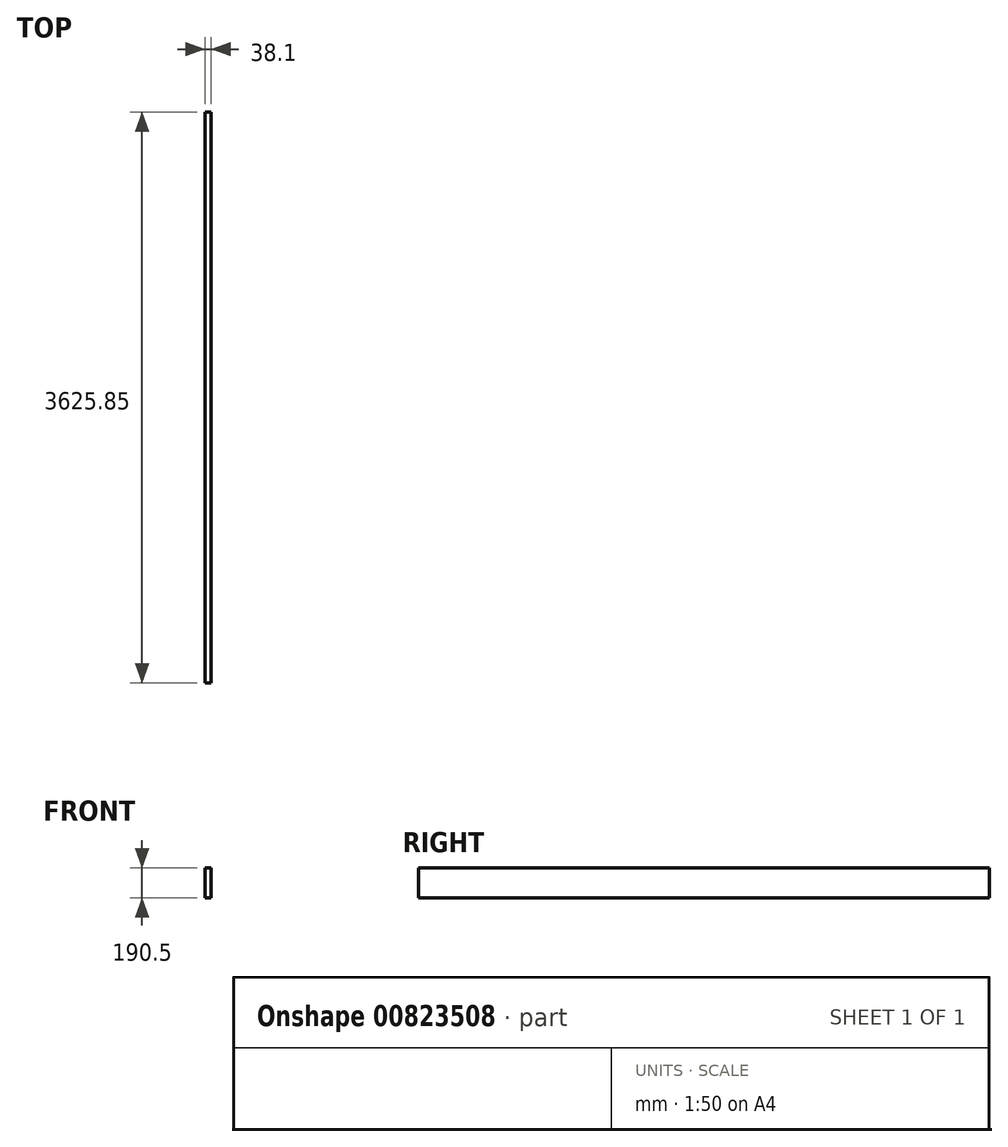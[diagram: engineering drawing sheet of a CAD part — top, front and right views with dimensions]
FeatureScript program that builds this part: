
annotation { "Feature Type Name" : "Feature", "Feature Type Description" : "" }
export const myFeature = defineFeature(function(context is Context, id is Id, definition is map)
    precondition{}
    {
        {
            var Q0;
            Q0=qCreatedBy(makeId("Front.planeOp"),FACE);
            var sketch = newSketch(context, id + "F0", { "sketchPlane" : qUnion([Q0])});
            skLineSegment(sketch, "E0.bottom", {"start": v(0, 0) * mm, "end": v(38.1, 0) * mm});
            skLineSegment(sketch, "E0.top", {"start": v(0, 190.5) * mm, "end": v(38.1, 190.5) * mm});
            skLineSegment(sketch, "E0.left", {"start": v(0, 0) * mm, "end": v(0, 190.5) * mm});
            skLineSegment(sketch, "E0.right", {"start": v(38.1, 0) * mm, "end": v(38.1, 190.5) * mm});
            skSolve(sketch);
        }
        {
            var Q0;
            Q0=qSketchRegion(id+"F0",true);
            extrude(context, id + "F1", {"entities" : qUnion([Q0]), "depth" : 3625.85 * mm, "offsetDistance" : 25.4 * mm});
        }
    });
